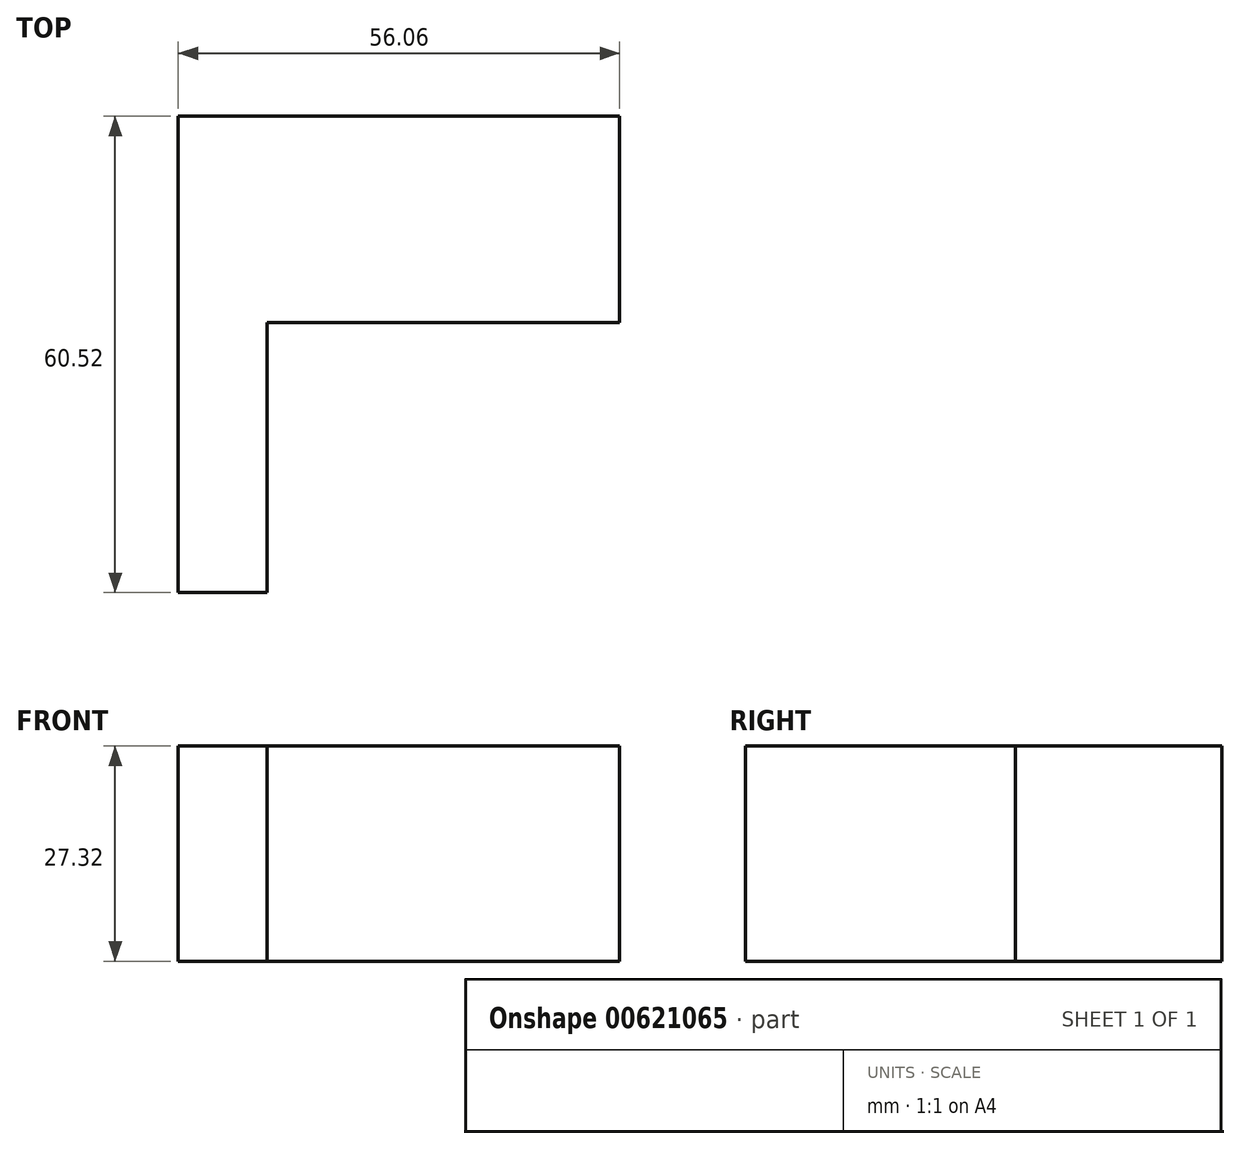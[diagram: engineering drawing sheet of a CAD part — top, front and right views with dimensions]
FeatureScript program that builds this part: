
annotation { "Feature Type Name" : "Feature", "Feature Type Description" : "" }
export const myFeature = defineFeature(function(context is Context, id is Id, definition is map)
    precondition{}
    {
        {
            var Q0;
            Q0=qCreatedBy(makeId("Top.planeOp"),FACE);
            var sketch = newSketch(context, id + "F0", { "sketchPlane" : qUnion([Q0])});
            skLineSegment(sketch, "E0.bottom", {"start": v(-8, 35.06) * mm, "end": v(-12.79, 35.06) * mm});
            skLineSegment(sketch, "E0.top", {"start": v(-8, 35.6) * mm, "end": v(-12.79, 35.6) * mm});
            skLineSegment(sketch, "E0.left", {"start": v(-8, 35.06) * mm, "end": v(-8, 35.6) * mm});
            skLineSegment(sketch, "E0.right", {"start": v(-12.79, 35.06) * mm, "end": v(-12.79, 35.6) * mm});
            skLineSegment(sketch, "E1.bottom", {"start": v(-24.1, 26.4) * mm, "end": v(-24.06, 26.4) * mm});
            skLineSegment(sketch, "E1.top", {"start": v(-24.1, 22.66) * mm, "end": v(-24.06, 22.66) * mm});
            skLineSegment(sketch, "E1.left", {"start": v(-24.1, 26.4) * mm, "end": v(-24.1, 22.66) * mm});
            skLineSegment(sketch, "E1.right", {"start": v(-24.06, 26.4) * mm, "end": v(-24.06, 22.66) * mm});
            skLineSegment(sketch, "E2.bottom", {"start": v(-11.3, 34.36) * mm, "end": v(44.76, 34.36) * mm});
            skLineSegment(sketch, "E2.top", {"start": v(-11.3, -26.16) * mm, "end": v(44.76, -26.16) * mm});
            skLineSegment(sketch, "E2.left", {"start": v(-11.3, 34.36) * mm, "end": v(-11.3, -26.16) * mm});
            skLineSegment(sketch, "E2.right", {"start": v(44.76, 34.36) * mm, "end": v(44.76, -26.16) * mm});
            skLineSegment(sketch, "E3.bottom", {"start": v(44.76, -26.16) * mm, "end": v(0, -26.16) * mm});
            skLineSegment(sketch, "E3.top", {"start": v(44.76, 8.14) * mm, "end": v(0, 8.14) * mm});
            skLineSegment(sketch, "E3.left", {"start": v(44.76, -26.16) * mm, "end": v(44.76, 8.14) * mm});
            skLineSegment(sketch, "E3.right", {"start": v(0, -26.16) * mm, "end": v(0, 8.14) * mm});
            skPoint(sketch, "E4.oppositeSnap0", {"position": v(0, -9) * mm});
            skLineSegment(sketch, "E4.bottom", {"start": v(0, -9) * mm, "end": v(30.25, -9) * mm});
            skLineSegment(sketch, "E4.top", {"start": v(0, -9) * mm, "end": v(30.25, -9) * mm});
            skLineSegment(sketch, "E4.left", {"start": v(0, -9) * mm, "end": v(0, -9) * mm});
            skLineSegment(sketch, "E4.right", {"start": v(30.25, -9) * mm, "end": v(30.25, -9) * mm});
            skSolve(sketch);
        }
        {
            var Q0;
            Q0=makeQuery(id+"F0.imprint","IMPRINT",FACE,{"disambiguationData":[TD([[makeQuery(id+"F0.imprint","IMPRINT",EDGE,{"derivedFrom":sQuery(id+"F0.wireOp",EDGE,"E2.bottom")}),-1.0]])]});
            extrude(context, id + "F1", {"entities" : qUnion([Q0]), "oppositeDirection" : true, "depth" : 27.32 * mm, "offsetDistance" : 25.4 * mm});
        }
    });
